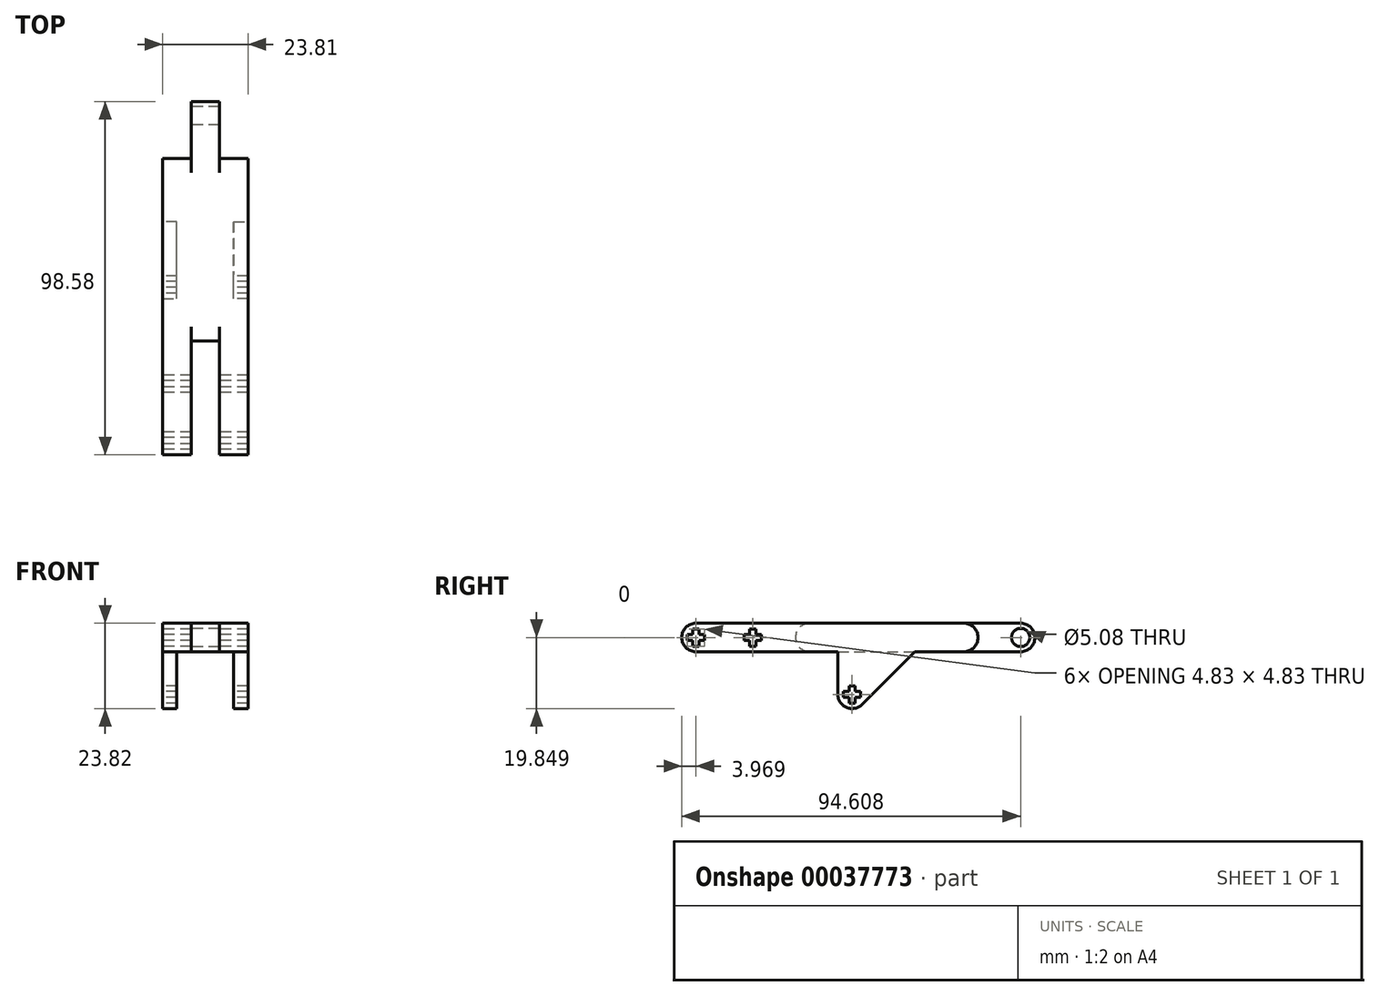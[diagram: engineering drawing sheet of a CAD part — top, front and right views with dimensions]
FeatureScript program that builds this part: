
annotation { "Feature Type Name" : "Feature", "Feature Type Description" : "" }
export const myFeature = defineFeature(function(context is Context, id is Id, definition is map)
    precondition{}
    {
        {
            var Q0;
            Q0=qCreatedBy(makeId("Top.planeOp"),FACE);
            var sketch = newSketch(context, id + "F0", { "sketchPlane" : qUnion([Q0])});
            skLineSegment(sketch, "E0.bottom", {"start": v(0, 0) * mm, "end": v(7.94, 0) * mm});
            skLineSegment(sketch, "E0.left", {"start": v(0, 0) * mm, "end": v(0, 82.7) * mm});
            skLineSegment(sketch, "E0.right", {"start": v(7.94, 0) * mm, "end": v(7.94, 31.75) * mm});
            skLineSegment(sketch, "E1.bottom", {"start": v(15.88, 0) * mm, "end": v(23.81, 0) * mm});
            skLineSegment(sketch, "E1.left", {"start": v(15.88, 0) * mm, "end": v(15.88, 31.75) * mm});
            skLineSegment(sketch, "E1.right", {"start": v(23.81, 0) * mm, "end": v(23.81, 82.7) * mm});
            skLineSegment(sketch, "E2", {"start": v(7.94, 31.75) * mm, "end": v(15.87, 31.75) * mm});
            skLineSegment(sketch, "E3", {"start": v(0, 82.7) * mm, "end": v(7.94, 82.7) * mm});
            skLineSegment(sketch, "E4", {"start": v(7.94, 82.7) * mm, "end": v(7.94, 98.58) * mm});
            skLineSegment(sketch, "E5", {"start": v(7.94, 98.58) * mm, "end": v(15.88, 98.58) * mm});
            skLineSegment(sketch, "E6", {"start": v(15.87, 98.58) * mm, "end": v(15.87, 82.7) * mm});
            skLineSegment(sketch, "E7", {"start": v(15.88, 82.7) * mm, "end": v(23.81, 82.7) * mm});
            skLineSegment(sketch, "E8", {"start": v(7.94, 82.7) * mm, "end": v(15.88, 82.7) * mm, "construction": true});
            skLineSegment(sketch, "E9", {"start": v(11.9, 82.7) * mm, "end": v(11.9, 31.75) * mm, "construction": true});
            skLineSegment(sketch, "E10", {"start": v(15.88, 0) * mm, "end": v(7.94, 0) * mm, "construction": true});
            skLineSegment(sketch, "E11", {"start": v(11.9, 0) * mm, "end": v(11.9, 8.24) * mm, "construction": true});
            skLineSegment(sketch, "E12", {"start": v(11.9, 8.24) * mm, "end": v(11.9, 18.1) * mm, "construction": true});
            skSolve(sketch);
        }
        {
            var Q0;
            Q0 = qSketchRegion(id + "F0", true);
            extrude(context, id + "F1", {"entities" : qUnion([Q0]), "depth" : 7.94 * mm});
        }
        {
            var Q0;
            Q0=makeQuery(id+"F1.opExtrude","CAP_FACE",FACE,{"disambiguationData":[OSD([sQuery(id+"F0.wireOp",EDGE,"E0.bottom"),sQuery(id+"F0.wireOp",EDGE,"E0.left"),sQuery(id+"F0.wireOp",EDGE,"E0.right"),sQuery(id+"F0.wireOp",EDGE,"E1.bottom"),sQuery(id+"F0.wireOp",EDGE,"E1.left"),sQuery(id+"F0.wireOp",EDGE,"E1.right"),sQuery(id+"F0.wireOp",EDGE,"E2"),sQuery(id+"F0.wireOp",EDGE,"E3"),sQuery(id+"F0.wireOp",EDGE,"E4"),sQuery(id+"F0.wireOp",EDGE,"E5"),sQuery(id+"F0.wireOp",EDGE,"E6"),sQuery(id+"F0.wireOp",EDGE,"E7")])],"isStart":true});
            var sketch = newSketch(context, id + "F2", { "sketchPlane" : qUnion([Q0])});
            skLineSegment(sketch, "E13", {"start": v(11.9, -31.75) * mm, "end": v(11.9, -47.55) * mm, "construction": true});
            skPoint(sketch, "E13.endSnap0", {"position": v(11.9, -31.75) * mm});
            skLineSegment(sketch, "E14", {"start": v(19.84, -47.55) * mm, "end": v(3.97, -47.55) * mm, "construction": true});
            skLineSegment(sketch, "E15.bottom", {"start": v(23.81, -43.58) * mm, "end": v(19.84, -43.58) * mm});
            skLineSegment(sketch, "E15.top", {"start": v(23.81, -51.51) * mm, "end": v(19.84, -51.51) * mm});
            skLineSegment(sketch, "E15.left", {"start": v(23.81, -43.58) * mm, "end": v(23.81, -51.51) * mm});
            skLineSegment(sketch, "E15.right", {"start": v(19.84, -43.58) * mm, "end": v(19.84, -51.51) * mm});
            skLineSegment(sketch, "E16.bottom", {"start": v(0, -43.58) * mm, "end": v(3.97, -43.58) * mm});
            skLineSegment(sketch, "E16.top", {"start": v(0, -51.51) * mm, "end": v(3.97, -51.51) * mm});
            skLineSegment(sketch, "E16.left", {"start": v(0, -43.58) * mm, "end": v(0, -51.51) * mm});
            skLineSegment(sketch, "E16.right", {"start": v(3.97, -43.58) * mm, "end": v(3.97, -51.51) * mm});
            skLineSegment(sketch, "E17", {"start": v(11.9, -47.55) * mm, "end": v(11.9, -94.6) * mm, "construction": true});
            skLineSegment(sketch, "E18", {"start": v(11.9, -94.6) * mm, "end": v(11.9, -98.58) * mm, "construction": true});
            skSolve(sketch);
        }
        {
            var Q0;
            Q0 = qSketchRegion(id + "F2", true);
            extrude(context, id + "F3", {"entities" : qUnion([Q0]), "operationType" : NewBodyOperationType.ADD, "depth" : 15.88 * mm});
        }
        {
            var Q0;
            Q0=makeQuery(id+"F1.opExtrude","CAP_EDGE",EDGE,{"disambiguationData":[OSD([sQuery(id+"F0.wireOp",EDGE,"E7")])],"isStart":true});
            var Q1;
            Q1=makeQuery(id+"F1.opExtrude","CAP_EDGE",EDGE,{"disambiguationData":[OSD([sQuery(id+"F0.wireOp",EDGE,"E7")])],"isStart":false});
            var Q2;
            Q2=makeQuery(id+"F1.opExtrude","CAP_EDGE",EDGE,{"disambiguationData":[OSD([sQuery(id+"F0.wireOp",EDGE,"E5")])],"isStart":true});
            var Q3;
            Q3=makeQuery(id+"F1.opExtrude","CAP_EDGE",EDGE,{"disambiguationData":[OSD([sQuery(id+"F0.wireOp",EDGE,"E5")])],"isStart":false});
            var Q4;
            Q4=makeQuery(id+"F1.opExtrude","CAP_EDGE",EDGE,{"disambiguationData":[OSD([sQuery(id+"F0.wireOp",EDGE,"E3")])],"isStart":true});
            var Q5;
            Q5=makeQuery(id+"F1.opExtrude","CAP_EDGE",EDGE,{"disambiguationData":[OSD([sQuery(id+"F0.wireOp",EDGE,"E3")])],"isStart":false});
            var Q6;
            Q6=makeQuery(id+"F3.opExtrude","CAP_EDGE",EDGE,{"disambiguationData":[OSD([sQuery(id+"F2.wireOp",EDGE,"E16.top")])],"isStart":false});
            var Q7;
            Q7=makeQuery(id+"F3.opExtrude","CAP_EDGE",EDGE,{"disambiguationData":[OSD([sQuery(id+"F2.wireOp",EDGE,"E16.bottom")])],"isStart":false});
            var Q8;
            Q8=makeQuery(id+"F3.opExtrude","CAP_EDGE",EDGE,{"disambiguationData":[OSD([sQuery(id+"F2.wireOp",EDGE,"E15.top")])],"isStart":false});
            var Q9;
            Q9=makeQuery(id+"F3.opExtrude","CAP_EDGE",EDGE,{"disambiguationData":[OSD([sQuery(id+"F2.wireOp",EDGE,"E15.bottom")])],"isStart":false});
            var Q10;
            Q10=makeQuery(id+"F1.opExtrude","CAP_EDGE",EDGE,{"disambiguationData":[OSD([sQuery(id+"F0.wireOp",EDGE,"E0.bottom")])],"isStart":true});
            var Q11;
            Q11=makeQuery(id+"F1.opExtrude","CAP_EDGE",EDGE,{"disambiguationData":[OSD([sQuery(id+"F0.wireOp",EDGE,"E0.bottom")])],"isStart":false});
            var Q12;
            Q12=makeQuery(id+"F1.opExtrude","CAP_EDGE",EDGE,{"disambiguationData":[OSD([sQuery(id+"F0.wireOp",EDGE,"E1.bottom")])],"isStart":false});
            var Q13;
            Q13=makeQuery(id+"F1.opExtrude","CAP_EDGE",EDGE,{"disambiguationData":[OSD([sQuery(id+"F0.wireOp",EDGE,"E1.bottom")])],"isStart":true});
            var Q14;
            Q14=makeQuery(id+"F1.opExtrude","CAP_EDGE",EDGE,{"disambiguationData":[OSD([sQuery(id+"F0.wireOp",EDGE,"E2")])],"isStart":false});
            var Q15;
            Q15=makeQuery(id+"F1.opExtrude","CAP_EDGE",EDGE,{"disambiguationData":[OSD([sQuery(id+"F0.wireOp",EDGE,"E2")])],"isStart":true});
            fillet(context, id + "F4", {"entities" : qUnion([Q0, Q1, Q2, Q3, Q4, Q5, Q6, Q7, Q8, Q9, Q10, Q11, Q12, Q13, Q14, Q15]), "radius" : 3.97 * mm, "tangentPropagation" : true, "allowEdgeOverflow" : false});
        }
        {
            var Q0;
            Q0=makeQuery(id+"F3.boolean.opBoolean","MERGE",FACE,{"derivedFrom":[makeQuery(id+"F1.opExtrude","SWEPT_FACE",FACE,{"disambiguationData":[OSD([sQuery(id+"F0.wireOp",EDGE,"E0.left")])]}),makeQuery(id+"F3.opExtrude","SWEPT_FACE",FACE,{"disambiguationData":[OSD([sQuery(id+"F2.wireOp",EDGE,"E16.left")])]})]});
            var sketch = newSketch(context, id + "F5", { "sketchPlane" : qUnion([Q0])});
            skLineSegment(sketch, "E19.rect.bottom", {"start": v(-1.56, 3.12) * mm, "end": v(-6.38, 3.12) * mm});
            skLineSegment(sketch, "E19.rect.top", {"start": v(-1.56, 4.81) * mm, "end": v(-6.38, 4.81) * mm});
            skLineSegment(sketch, "E19.rect.left", {"start": v(-1.56, 3.12) * mm, "end": v(-1.56, 4.81) * mm});
            skLineSegment(sketch, "E19.rect.right", {"start": v(-6.38, 3.12) * mm, "end": v(-6.38, 4.81) * mm});
            skPoint(sketch, "E19.rect.middle", {"position": v(-3.97, 3.97) * mm});
            skLineSegment(sketch, "E20.rect.bottom", {"start": v(-4.81, 6.38) * mm, "end": v(-3.12, 6.38) * mm});
            skLineSegment(sketch, "E20.rect.top", {"start": v(-4.81, 1.56) * mm, "end": v(-3.12, 1.56) * mm});
            skLineSegment(sketch, "E20.rect.left", {"start": v(-4.81, 6.38) * mm, "end": v(-4.81, 1.56) * mm});
            skLineSegment(sketch, "E20.rect.right", {"start": v(-3.12, 6.38) * mm, "end": v(-3.12, 1.56) * mm});
            skLineSegment(sketch, "E21.rect.bottom", {"start": v(-48.4, -9.5) * mm, "end": v(-46.7, -9.5) * mm});
            skLineSegment(sketch, "E21.rect.top", {"start": v(-48.4, -14.32) * mm, "end": v(-46.7, -14.32) * mm});
            skLineSegment(sketch, "E21.rect.left", {"start": v(-48.4, -9.5) * mm, "end": v(-48.4, -14.32) * mm});
            skLineSegment(sketch, "E21.rect.right", {"start": v(-46.7, -9.5) * mm, "end": v(-46.7, -14.32) * mm});
            skPoint(sketch, "E21.rect.middle", {"position": v(-47.55, -11.9) * mm});
            skLineSegment(sketch, "E22.rect.bottom", {"start": v(-49.96, -11.06) * mm, "end": v(-45.13, -11.06) * mm});
            skLineSegment(sketch, "E22.rect.top", {"start": v(-49.96, -12.75) * mm, "end": v(-45.13, -12.75) * mm});
            skLineSegment(sketch, "E22.rect.left", {"start": v(-49.96, -11.06) * mm, "end": v(-49.96, -12.75) * mm});
            skLineSegment(sketch, "E22.rect.right", {"start": v(-45.13, -11.06) * mm, "end": v(-45.13, -12.75) * mm});
            skLineSegment(sketch, "E23", {"start": v(-3.97, 3.97) * mm, "end": v(-19.84, 3.97) * mm, "construction": true});
            skLineSegment(sketch, "E24.rect.bottom", {"start": v(-20.69, 1.56) * mm, "end": v(-19, 1.56) * mm});
            skLineSegment(sketch, "E24.rect.top", {"start": v(-20.69, 6.38) * mm, "end": v(-19, 6.38) * mm});
            skLineSegment(sketch, "E24.rect.left", {"start": v(-20.69, 1.56) * mm, "end": v(-20.69, 6.38) * mm});
            skLineSegment(sketch, "E24.rect.right", {"start": v(-19, 1.56) * mm, "end": v(-19, 6.38) * mm});
            skPoint(sketch, "E24.rect.middle", {"position": v(-19.84, 3.97) * mm});
            skLineSegment(sketch, "E25.rect.bottom", {"start": v(-22.26, 4.81) * mm, "end": v(-17.43, 4.81) * mm});
            skLineSegment(sketch, "E25.rect.top", {"start": v(-22.26, 3.12) * mm, "end": v(-17.43, 3.12) * mm});
            skLineSegment(sketch, "E25.rect.left", {"start": v(-22.26, 4.81) * mm, "end": v(-22.26, 3.12) * mm});
            skLineSegment(sketch, "E25.rect.right", {"start": v(-17.43, 4.81) * mm, "end": v(-17.43, 3.12) * mm});
            skCircle(sketch, "E26", {"center": v(-94.6, 3.97) * mm, "radius": 2.54 * mm});
            skSolve(sketch);
        }
        {
            var Q0;
            Q0 = qSketchRegion(id + "F5", true);
            var Q1;
            Q1=makeQuery(id+"F3.boolean.opBoolean","MERGE",FACE,{"derivedFrom":[makeQuery(id+"F1.opExtrude","SWEPT_FACE",FACE,{"disambiguationData":[OSD([sQuery(id+"F0.wireOp",EDGE,"E1.right")])]}),makeQuery(id+"F3.opExtrude","SWEPT_FACE",FACE,{"disambiguationData":[OSD([sQuery(id+"F2.wireOp",EDGE,"E15.left")])]})]});
            extrude(context, id + "F6", {"entities" : qUnion([Q0]), "operationType" : NewBodyOperationType.REMOVE, "endBound" : BoundingType.UP_TO_SURFACE, "oppositeDirection" : true, "endBoundEntityFace" : qUnion([Q1]), "depth" : 25.4 * mm});
        }
        {
            var Q0;
            Q0=makeQuery(id+"F3.boolean.opBoolean","MERGE",FACE,{"derivedFrom":[makeQuery(id+"F1.opExtrude","SWEPT_FACE",FACE,{"disambiguationData":[OSD([sQuery(id+"F0.wireOp",EDGE,"E0.left")])]}),makeQuery(id+"F3.opExtrude","SWEPT_FACE",FACE,{"disambiguationData":[OSD([sQuery(id+"F2.wireOp",EDGE,"E16.left")])]})]});
            var sketch = newSketch(context, id + "F7", { "sketchPlane" : qUnion([Q0])});
            skLineSegment(sketch, "E27", {"start": v(-50.35, -14.71) * mm, "end": v(-65.06, 0) * mm});
            skLineSegment(sketch, "E28", {"start": v(-65.06, 0) * mm, "end": v(-51.51, 0) * mm});
            skLineSegment(sketch, "E29", {"start": v(-51.51, 0) * mm, "end": v(-51.51, -11.9) * mm});
            skArc(sketch, "E30", {"start": v(-51.51, -11.9) * mm, "mid": v(-51.21, -13.43) * mm, "end": v(-50.35, -14.71) * mm});
            skSolve(sketch);
        }
        {
            var Q0;
            Q0 = qSketchRegion(id + "F7", true);
            var Q1;
            Q1=makeQuery(id+"F3.opExtrude","SWEPT_FACE",FACE,{"disambiguationData":[OSD([sQuery(id+"F2.wireOp",EDGE,"E16.right")])]});
            extrude(context, id + "F8", {"entities" : qUnion([Q0]), "operationType" : NewBodyOperationType.ADD, "endBound" : BoundingType.UP_TO_SURFACE, "oppositeDirection" : true, "endBoundEntityFace" : qUnion([Q1]), "depth" : 25.4 * mm});
        }
        {
            var Q0;
            Q0=makeQuery(id+"F3.boolean.opBoolean","MERGE",FACE,{"derivedFrom":[makeQuery(id+"F1.opExtrude","SWEPT_FACE",FACE,{"disambiguationData":[OSD([sQuery(id+"F0.wireOp",EDGE,"E1.right")])]}),makeQuery(id+"F3.opExtrude","SWEPT_FACE",FACE,{"disambiguationData":[OSD([sQuery(id+"F2.wireOp",EDGE,"E15.left")])]})]});
            var sketch = newSketch(context, id + "F9", { "sketchPlane" : qUnion([Q0])});
            skLineSegment(sketch, "E31", {"start": v(50.35, -14.71) * mm, "end": v(65.06, 0) * mm});
            skLineSegment(sketch, "E32", {"start": v(65.06, 0) * mm, "end": v(51.51, 0) * mm});
            skLineSegment(sketch, "E33", {"start": v(51.51, 0) * mm, "end": v(51.51, -11.9) * mm});
            skArc(sketch, "E34", {"start": v(50.35, -14.71) * mm, "mid": v(51.21, -13.43) * mm, "end": v(51.51, -11.9) * mm});
            skSolve(sketch);
        }
        {
            var Q0;
            Q0 = qSketchRegion(id + "F9", true);
            var Q1;
            Q1=makeQuery(id+"F3.opExtrude","SWEPT_FACE",FACE,{"disambiguationData":[OSD([sQuery(id+"F2.wireOp",EDGE,"E15.right")])]});
            extrude(context, id + "F10", {"entities" : qUnion([Q0]), "operationType" : NewBodyOperationType.ADD, "endBound" : BoundingType.UP_TO_SURFACE, "oppositeDirection" : true, "endBoundEntityFace" : qUnion([Q1]), "depth" : 25.4 * mm});
        }
    });
